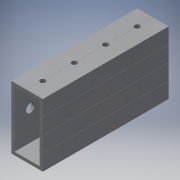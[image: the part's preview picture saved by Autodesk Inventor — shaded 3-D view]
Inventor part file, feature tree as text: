
AUTODESK INVENTOR PART (.ipt)
format: ipt  version: 2017 (Build 210142000, 142)  size: 472,064 bytes
history: native  units: in
note: dims shown in document units (in); Inventor stores cm internally (conversion verified against a paired STEP export)
features: other x8, reference x5, sketch x3, extrude x3, plane x1
ambient origin geometry x8: Origin, YZ Plane, XZ Plane, XY Plane, X Axis, Y Axis, Z Axis, Center Point
bodies: Solid1 (feature_tree)
feature tree (20):
  sketch  "Sketch1"  dims[d0=4.0in d3=3.0in d4=0.94in d12=0.94in d13=3.0in]
  extrude  "Extrusion2"  Depth=4.0in
  extrude  "Extrusion3"  Depth=1.0in TaperAngle=0.0deg
  plane  "Work Plane4"
  extrude  "Extrusion4"  Depth=1.0in
  sketch  "Sketch2"  dims[d30=1.0in d31=0.0in d32=1.0in d33=0.0in]
  reference  "Reference1"
  reference  "Reference2"
  reference  "Reference3"
  reference  "Reference4"
  sketch  "Sketch3"  dims[d34=0.5in d35=0.0in d21=1.0in d22=1.0in]
  reference  "Reference5"
  other  "Cut-Extrude2"
  other  "<userpath>\Documents\GitHub\2898-STEAMworks-CAD\2898-17-A-0100\SideFrame.iam"
  other  "SideFrame.iam"
  other  "WCP_DS_Gearbox:1"
  parser-record x1  (decoder bookkeeping rows leaked as tree rows — omitted from the tree; the rows remain in map.json)
  other  "2898-17-A-0000.iam"
  other  "2898-17-A-0600:1"
  other  "Hopper_Net_Frame_Gusset:5"
note: 1 file-system path scrubbed to <path> (originals preserved in map.json)
